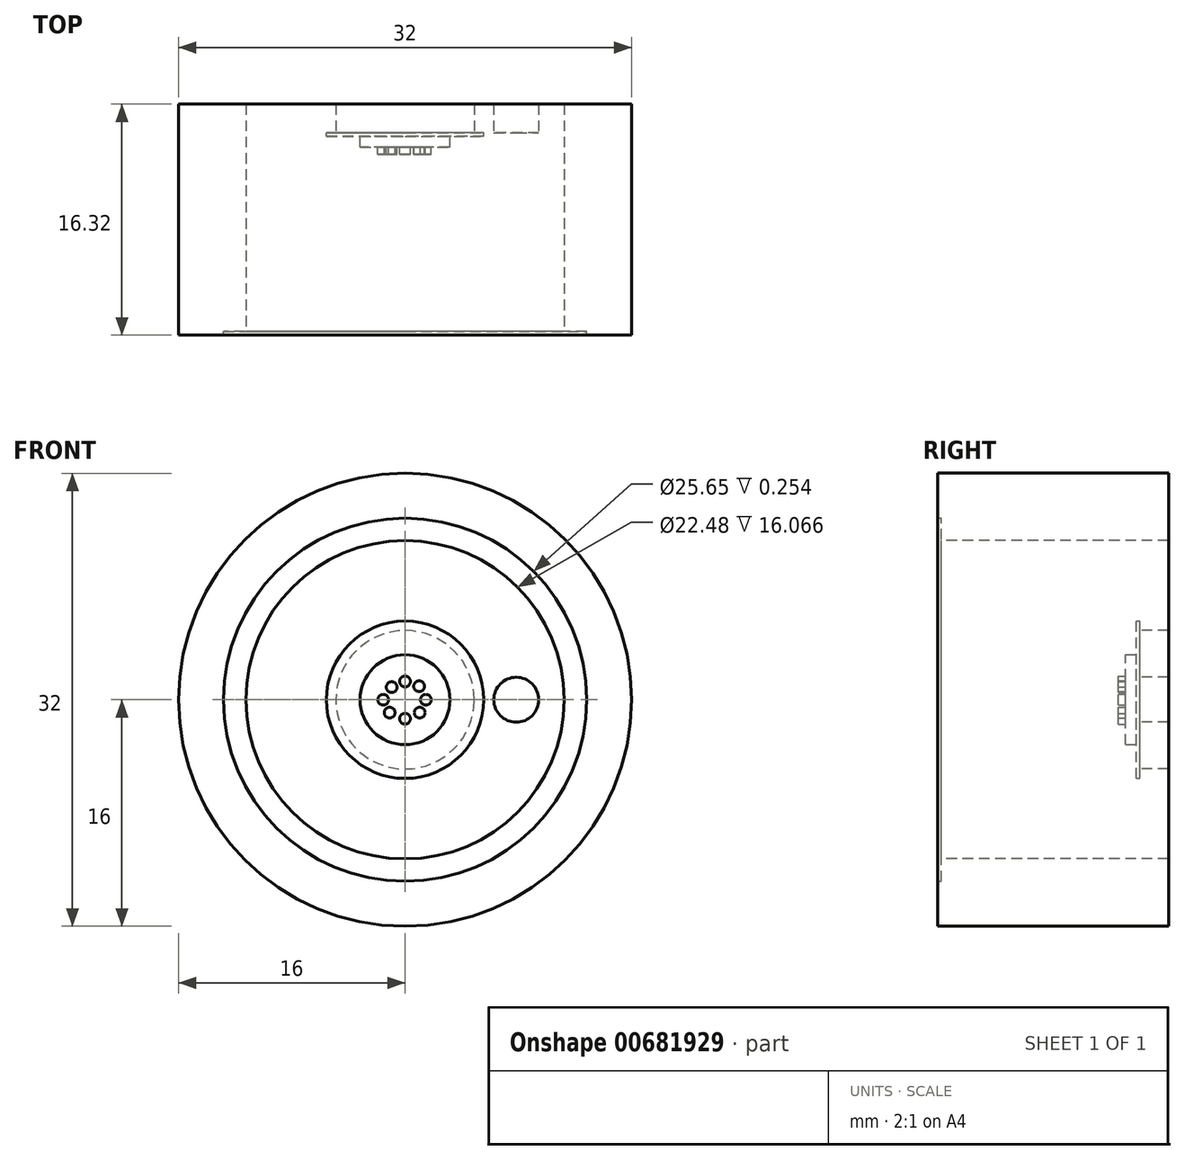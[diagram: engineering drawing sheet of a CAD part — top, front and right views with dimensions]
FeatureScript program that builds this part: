
annotation { "Feature Type Name" : "Feature", "Feature Type Description" : "" }
export const myFeature = defineFeature(function(context is Context, id is Id, definition is map)
    precondition{}
    {
        {
            var Q0;
            Q0=qCreatedBy(makeId("Front.planeOp"),FACE);
            var sketch = newSketch(context, id + "F0", { "sketchPlane" : qUnion([Q0])});
            skCircle(sketch, "E0", {"center": v(0, 0) * mm, "radius": 16 * mm});
            skSolve(sketch);
        }
        {
            var Q0;
            Q0=makeQuery(id+"F0.imprint","IMPRINT",FACE,{"disambiguationData":[TD([[makeQuery(id+"F0.imprint","IMPRINT",EDGE,{"derivedFrom":sQuery(id+"F0.wireOp",EDGE,"E0")}),1.0]])]});
            extrude(context, id + "F1", {"entities" : qUnion([Q0]), "oppositeDirection" : true, "depth" : 2.03 * mm, "offsetDistance" : 25.4 * mm});
        }
        {
            var Q0;
            Q0=makeQuery(id+"F1.opExtrude","CAP_FACE",FACE,{"disambiguationData":[OSD([sQuery(id+"F0.wireOp",EDGE,"E0")])],"isStart":true});
            var sketch = newSketch(context, id + "F2", { "sketchPlane" : qUnion([Q0])});
            skCircle(sketch, "E1", {"center": v(0, 0) * mm, "radius": 11.24 * mm});
            skCircle(sketch, "E2", {"center": v(0, 0) * mm, "radius": 4.89 * mm});
            skLineSegment(sketch, "E3", {"start": v(-11.24, 0) * mm, "end": v(11.24, 0) * mm});
            skCircle(sketch, "E4", {"center": v(-8.31, 0) * mm, "radius": 1.59 * mm});
            skCircle(sketch, "E5", {"center": v(7.86, 0) * mm, "radius": 1.59 * mm});
            skCircle(sketch, "E6", {"center": v(0, 7.92) * mm, "radius": 1.59 * mm});
            skCircle(sketch, "E7", {"center": v(0, -7.97) * mm, "radius": 1.59 * mm});
            skCircle(sketch, "E8", {"center": v(-5.86, -4.96) * mm, "radius": 1.59 * mm});
            skCircle(sketch, "E9", {"center": v(5.6, -5.31) * mm, "radius": 1.59 * mm});
            skCircle(sketch, "E10", {"center": v(-5.41, 5.4) * mm, "radius": 1.59 * mm});
            skCircle(sketch, "E11", {"center": v(5.37, 5.57) * mm, "radius": 1.59 * mm});
            skSolve(sketch);
        }
        {
            var Q0;
            Q0=makeQuery(id+"F1.opExtrude","CAP_FACE",FACE,{"disambiguationData":[OSD([sQuery(id+"F0.wireOp",EDGE,"E0")])],"isStart":true});
            var sketch = newSketch(context, id + "F3", { "sketchPlane" : qUnion([Q0])});
            skCircle(sketch, "E12", {"center": v(0, 0) * mm, "radius": 12.83 * mm});
            skCircle(sketch, "E13", {"center": v(0, 0) * mm, "radius": 11.23 * mm});
            skSolve(sketch);
        }
        {
            var Q0;
            Q0=makeQuery(id+"F3.imprint","IMPRINT",FACE,{"disambiguationData":[TD([[makeQuery(id+"F3.imprint","IMPRINT",EDGE,{"derivedFrom":sQuery(id+"F3.wireOp",EDGE,"E12")}),1.0]])]});
            extrude(context, id + "F4", {"entities" : qUnion([Q0]), "operationType" : NewBodyOperationType.REMOVE, "oppositeDirection" : true, "depth" : 0.25 * mm, "offsetDistance" : 25.4 * mm});
        }
        {
            var Q0;
            Q0=makeQuery(id+"F2.imprint","IMPRINT",FACE,{"disambiguationData":[TD([[makeQuery(id+"F2.imprint","IMPRINT",EDGE,{"derivedFrom":sQuery(id+"F2.wireOp",EDGE,"E7")}),1.0]])]});
            var Q1;
            Q1=makeQuery(id+"F2.imprint","IMPRINT",FACE,{"disambiguationData":[TD([[makeQuery(id+"F2.imprint","IMPRINT",EDGE,{"derivedFrom":sQuery(id+"F2.wireOp",EDGE,"E8")}),1.0]])]});
            var Q2;
            {var subQ0=sQuery(id+"F2.wireOp",EDGE,"E4");var subQ1=sQuery(id+"F2.wireOp",EDGE,"E3");var subQ2=makeQuery(id+"F2.imprint","INTERSECT",VERTEX,{"disambiguationData":[OD(0.0)],"derivedFrom":[subQ1,subQ0]});Q2=makeQuery(id+"F2.imprint","IMPRINT",FACE,{"disambiguationData":[TD([[makeQuery(id+"F2.imprint","IMPRINT",EDGE,{"disambiguationData":[TD([[subQ2,-1.0]])],"derivedFrom":subQ1}),-1.0]])]});}
            var Q3;
            {var subQ0=sQuery(id+"F2.wireOp",EDGE,"E4");var subQ1=sQuery(id+"F2.wireOp",EDGE,"E3");var subQ2=makeQuery(id+"F2.imprint","INTERSECT",VERTEX,{"disambiguationData":[OD(0.0)],"derivedFrom":[subQ1,subQ0]});Q3=makeQuery(id+"F2.imprint","IMPRINT",FACE,{"disambiguationData":[TD([[makeQuery(id+"F2.imprint","IMPRINT",EDGE,{"disambiguationData":[TD([[subQ2,-1.0]])],"derivedFrom":subQ1}),1.0]])]});}
            var Q4;
            Q4=makeQuery(id+"F2.imprint","IMPRINT",FACE,{"disambiguationData":[TD([[makeQuery(id+"F2.imprint","IMPRINT",EDGE,{"derivedFrom":sQuery(id+"F2.wireOp",EDGE,"E10")}),1.0]])]});
            var Q5;
            Q5=makeQuery(id+"F2.imprint","IMPRINT",FACE,{"disambiguationData":[TD([[makeQuery(id+"F2.imprint","IMPRINT",EDGE,{"derivedFrom":sQuery(id+"F2.wireOp",EDGE,"E6")}),1.0]])]});
            var Q6;
            Q6=makeQuery(id+"F2.imprint","IMPRINT",FACE,{"disambiguationData":[TD([[makeQuery(id+"F2.imprint","IMPRINT",EDGE,{"derivedFrom":sQuery(id+"F2.wireOp",EDGE,"E11")}),1.0]])]});
            var Q7;
            {var subQ0=sQuery(id+"F2.wireOp",EDGE,"E5");var subQ1=sQuery(id+"F2.wireOp",EDGE,"E3");var subQ2=makeQuery(id+"F2.imprint","INTERSECT",VERTEX,{"disambiguationData":[OD(0.0)],"derivedFrom":[subQ1,subQ0]});Q7=makeQuery(id+"F2.imprint","IMPRINT",FACE,{"disambiguationData":[TD([[makeQuery(id+"F2.imprint","IMPRINT",EDGE,{"disambiguationData":[TD([[subQ2,-1.0]])],"derivedFrom":subQ1}),1.0]])]});}
            var Q8;
            {var subQ0=sQuery(id+"F2.wireOp",EDGE,"E5");var subQ1=sQuery(id+"F2.wireOp",EDGE,"E3");var subQ2=makeQuery(id+"F2.imprint","INTERSECT",VERTEX,{"disambiguationData":[OD(0.0)],"derivedFrom":[subQ1,subQ0]});Q8=makeQuery(id+"F2.imprint","IMPRINT",FACE,{"disambiguationData":[TD([[makeQuery(id+"F2.imprint","IMPRINT",EDGE,{"disambiguationData":[TD([[subQ2,-1.0]])],"derivedFrom":subQ1}),-1.0]])]});}
            var Q9;
            Q9=makeQuery(id+"F2.imprint","IMPRINT",FACE,{"disambiguationData":[TD([[makeQuery(id+"F2.imprint","IMPRINT",EDGE,{"derivedFrom":sQuery(id+"F2.wireOp",EDGE,"E9")}),1.0]])]});
            extrude(context, id + "F5", {"entities" : qUnion([Q0, Q1, Q2, Q3, Q4, Q5, Q6, Q7, Q8, Q9]), "operationType" : NewBodyOperationType.REMOVE, "oppositeDirection" : true, "depth" : 2.03 * mm, "offsetDistance" : 25.4 * mm});
        }
        {
            var Q0;
            Q0=makeQuery(id+"F4.boolean.opBoolean","SPLIT",FACE,{"disambiguationData":[TD([makeQuery(id+"F4.opExtrude","SWEPT_FACE",FACE,{"disambiguationData":[OSD([sQuery(id+"F3.wireOp",EDGE,"E13")])]})])],"derivedFrom":makeQuery(id+"F1.opExtrude","CAP_FACE",FACE,{"disambiguationData":[OSD([sQuery(id+"F0.wireOp",EDGE,"E0")])],"isStart":true})});
            var sketch = newSketch(context, id + "F6", { "sketchPlane" : qUnion([Q0])});
            skCircle(sketch, "E14", {"center": v(0, 0) * mm, "radius": 5.56 * mm});
            skSolve(sketch);
        }
        {
            var Q0;
            Q0=makeQuery(id+"F6.imprint","IMPRINT",FACE,{"disambiguationData":[TD([[makeQuery(id+"F6.imprint","IMPRINT",EDGE,{"derivedFrom":sQuery(id+"F6.wireOp",EDGE,"E14")}),1.0]])]});
            extrude(context, id + "F7", {"entities" : qUnion([Q0]), "operationType" : NewBodyOperationType.ADD, "depth" : 0.25 * mm, "offsetDistance" : 25.4 * mm});
        }
        {
            var Q0;
            Q0=makeQuery(id+"F7.opExtrude","CAP_FACE",FACE,{"disambiguationData":[OSD([sQuery(id+"F6.wireOp",EDGE,"E14")])],"isStart":false});
            var sketch = newSketch(context, id + "F8", { "sketchPlane" : qUnion([Q0])});
            skCircle(sketch, "E15", {"center": v(0, 0) * mm, "radius": 3.17 * mm});
            skSolve(sketch);
        }
        {
            var Q0;
            Q0=makeQuery(id+"F8.imprint","IMPRINT",FACE,{"disambiguationData":[TD([[makeQuery(id+"F8.imprint","IMPRINT",EDGE,{"derivedFrom":sQuery(id+"F8.wireOp",EDGE,"E15")}),1.0]])]});
            extrude(context, id + "F9", {"entities" : qUnion([Q0]), "operationType" : NewBodyOperationType.ADD, "depth" : 0.76 * mm, "offsetDistance" : 25.4 * mm});
        }
        {
            var Q0;
            Q0=makeQuery(id+"F9.opExtrude","CAP_FACE",FACE,{"disambiguationData":[OSD([sQuery(id+"F8.wireOp",EDGE,"E15")])],"isStart":false});
            var sketch = newSketch(context, id + "F10", { "sketchPlane" : qUnion([Q0])});
            skCircle(sketch, "E16", {"center": v(0, 1.3) * mm, "radius": 0.38 * mm});
            skCircle(sketch, "E17", {"center": v(1.47, 0) * mm, "radius": 0.38 * mm});
            skCircle(sketch, "E18", {"center": v(0, -1.34) * mm, "radius": 0.38 * mm});
            skCircle(sketch, "E19", {"center": v(-1.54, 0) * mm, "radius": 0.38 * mm});
            skCircle(sketch, "E20", {"center": v(-0.95, 0.9) * mm, "radius": 0.38 * mm});
            skCircle(sketch, "E21", {"center": v(1, 0.96) * mm, "radius": 0.38 * mm});
            skCircle(sketch, "E22", {"center": v(1.03, -0.9) * mm, "radius": 0.38 * mm});
            skCircle(sketch, "E23", {"center": v(-1.09, -0.9) * mm, "radius": 0.38 * mm});
            skSolve(sketch);
        }
        {
            var Q0;
            Q0=makeQuery(id+"F10.imprint","IMPRINT",FACE,{"disambiguationData":[TD([[makeQuery(id+"F10.imprint","IMPRINT",EDGE,{"derivedFrom":sQuery(id+"F10.wireOp",EDGE,"E19")}),1.0]])]});
            var Q1;
            Q1=makeQuery(id+"F10.imprint","IMPRINT",FACE,{"disambiguationData":[TD([[makeQuery(id+"F10.imprint","IMPRINT",EDGE,{"derivedFrom":sQuery(id+"F10.wireOp",EDGE,"E20")}),1.0]])]});
            var Q2;
            Q2=makeQuery(id+"F10.imprint","IMPRINT",FACE,{"disambiguationData":[TD([[makeQuery(id+"F10.imprint","IMPRINT",EDGE,{"derivedFrom":sQuery(id+"F10.wireOp",EDGE,"E16")}),1.0]])]});
            var Q3;
            Q3=makeQuery(id+"F10.imprint","IMPRINT",FACE,{"disambiguationData":[TD([[makeQuery(id+"F10.imprint","IMPRINT",EDGE,{"derivedFrom":sQuery(id+"F10.wireOp",EDGE,"E21")}),1.0]])]});
            var Q4;
            Q4=makeQuery(id+"F10.imprint","IMPRINT",FACE,{"disambiguationData":[TD([[makeQuery(id+"F10.imprint","IMPRINT",EDGE,{"derivedFrom":sQuery(id+"F10.wireOp",EDGE,"E17")}),1.0]])]});
            var Q5;
            Q5=makeQuery(id+"F10.imprint","IMPRINT",FACE,{"disambiguationData":[TD([[makeQuery(id+"F10.imprint","IMPRINT",EDGE,{"derivedFrom":sQuery(id+"F10.wireOp",EDGE,"E22")}),1.0]])]});
            var Q6;
            Q6=makeQuery(id+"F10.imprint","IMPRINT",FACE,{"disambiguationData":[TD([[makeQuery(id+"F10.imprint","IMPRINT",EDGE,{"derivedFrom":sQuery(id+"F10.wireOp",EDGE,"E18")}),1.0]])]});
            var Q7;
            Q7=makeQuery(id+"F10.imprint","IMPRINT",FACE,{"disambiguationData":[TD([[makeQuery(id+"F10.imprint","IMPRINT",EDGE,{"derivedFrom":sQuery(id+"F10.wireOp",EDGE,"E23")}),1.0]])]});
            extrude(context, id + "F11", {"entities" : qUnion([Q0, Q1, Q2, Q3, Q4, Q5, Q6, Q7]), "operationType" : NewBodyOperationType.ADD, "depth" : 0.5 * mm, "offsetDistance" : 25.4 * mm});
        }
        {
            var Q0;
            {var subQ0=sQuery(id+"F0.wireOp",EDGE,"E0");Q0=makeQuery(id+"F4.boolean.opBoolean","SPLIT",FACE,{"disambiguationData":[TD([makeQuery(id+"F1.opExtrude","SWEPT_FACE",FACE,{"disambiguationData":[OSD([subQ0])]})])],"derivedFrom":makeQuery(id+"F1.opExtrude","CAP_FACE",FACE,{"disambiguationData":[OSD([subQ0])],"isStart":true})});}
            var Q1;
            Q1=makeQuery(id+"F4.boolean.opBoolean","COPY",FACE,{"derivedFrom":makeQuery(id+"F4.opExtrude","CAP_FACE",FACE,{"disambiguationData":[OSD([sQuery(id+"F3.wireOp",EDGE,"E12"),sQuery(id+"F3.wireOp",EDGE,"E13")])],"isStart":false})});
            extrude(context, id + "F12", {"entities" : qUnion([Q0, Q1]), "operationType" : NewBodyOperationType.ADD, "depth" : 14.29 * mm, "offsetDistance" : 25.4 * mm});
        }
    });
